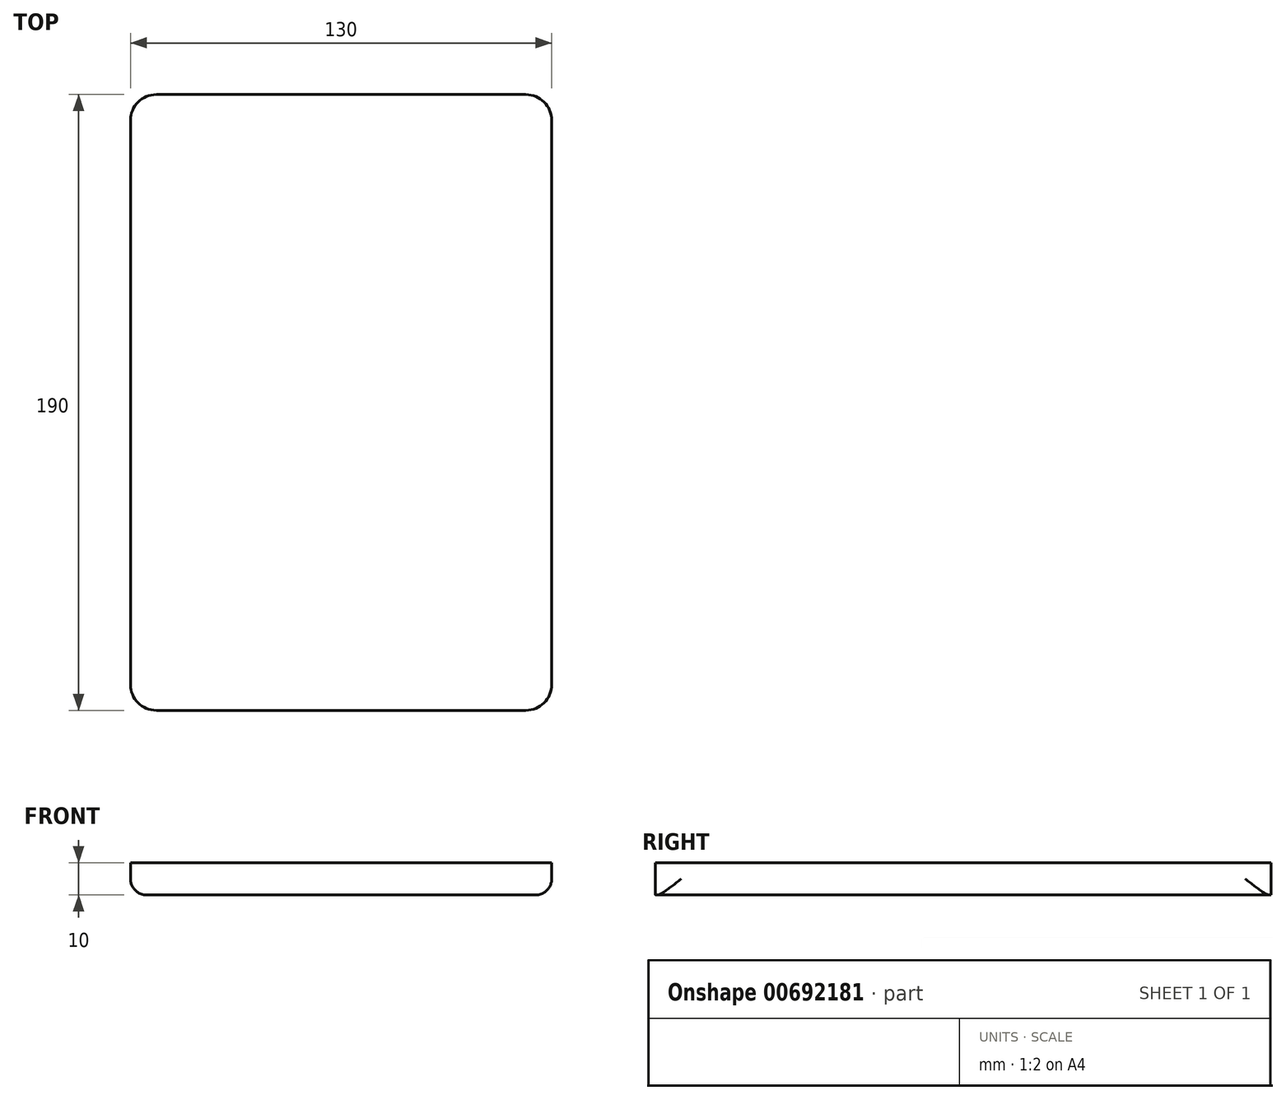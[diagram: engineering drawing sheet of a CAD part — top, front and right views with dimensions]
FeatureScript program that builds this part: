
annotation { "Feature Type Name" : "Feature", "Feature Type Description" : "" }
export const myFeature = defineFeature(function(context is Context, id is Id, definition is map)
    precondition{}
    {
        {
            var Q0;
            Q0=qCreatedBy(makeId("Top.planeOp"),FACE);
            var sketch = newSketch(context, id + "F0", { "sketchPlane" : qUnion([Q0])});
            skLineSegment(sketch, "E0.bottom", {"start": v(-65, -95) * mm, "end": v(65, -95) * mm});
            skLineSegment(sketch, "E0.top", {"start": v(-65, 95) * mm, "end": v(65, 95) * mm});
            skLineSegment(sketch, "E0.left", {"start": v(-65, -95) * mm, "end": v(-65, 95) * mm});
            skLineSegment(sketch, "E0.right", {"start": v(65, -95) * mm, "end": v(65, 95) * mm});
            skPoint(sketch, "E0.middle", {"position": v(0, 0) * mm});
            skSolve(sketch);
        }
        {
            var Q0;
            Q0 = qSketchRegion(id + "F0", true);
            extrude(context, id + "F1", {"entities" : qUnion([Q0]), "depth" : 10 * mm, "offsetDistance" : 25 * mm});
        }
        {
            var Q0;
            Q0=makeQuery(id+"F1.opExtrude","SWEPT_EDGE",EDGE,{"disambiguationData":[OSD([sQuery(id+"F0.wireOp",EDGE,"E0.top"),sQuery(id+"F0.wireOp",EDGE,"E0.left")])]});
            var Q1;
            Q1=makeQuery(id+"F1.opExtrude","SWEPT_EDGE",EDGE,{"disambiguationData":[OSD([sQuery(id+"F0.wireOp",EDGE,"E0.top"),sQuery(id+"F0.wireOp",EDGE,"E0.right")])]});
            var Q2;
            Q2=makeQuery(id+"F1.opExtrude","SWEPT_EDGE",EDGE,{"disambiguationData":[OSD([sQuery(id+"F0.wireOp",EDGE,"E0.bottom"),sQuery(id+"F0.wireOp",EDGE,"E0.right")])]});
            var Q3;
            Q3=makeQuery(id+"F1.opExtrude","SWEPT_EDGE",EDGE,{"disambiguationData":[OSD([sQuery(id+"F0.wireOp",EDGE,"E0.bottom"),sQuery(id+"F0.wireOp",EDGE,"E0.left")])]});
            fillet(context, id + "F2", {"entities" : qUnion([Q0, Q1, Q2, Q3]), "radius" : 8 * mm, "tangentPropagation" : true, "allowEdgeOverflow" : false});
        }
        {
            var Q0;
            Q0=makeQuery(id+"F1.opExtrude","CAP_EDGE",EDGE,{"disambiguationData":[OSD([sQuery(id+"F0.wireOp",EDGE,"E0.right")])],"isStart":true});
            var Q1;
            Q1=makeQuery(id+"F1.opExtrude","CAP_EDGE",EDGE,{"disambiguationData":[OSD([sQuery(id+"F0.wireOp",EDGE,"E0.left")])],"isStart":true});
            fillet(context, id + "F3", {"entities" : qUnion([Q0, Q1]), "radius" : 5 * mm, "allowEdgeOverflow" : false});
        }
    });
